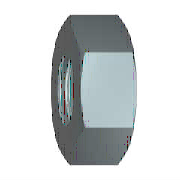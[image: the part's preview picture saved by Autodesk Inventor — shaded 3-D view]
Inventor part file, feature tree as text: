
AUTODESK INVENTOR PART (.ipt)
format: ipt  version: 2024 (Build 280153000, 153)  size: 162,304 bytes
history: native  units: mm (DEFAULTED — no unit token found)
features: other x2, extrude x1, hole x1, plane x1
ambient origin geometry x7: Origin, YZ Plane, XZ Plane, X Axis, Y Axis, Z Axis, Center Point
bodies: Solid1 (feature_tree)
feature tree (5):
  extrude  "Базовый элемент"  Depth=2.886751mm
  other  "Фаска1"
  hole  "Резьба"  [1 undecoded]
  other  "Work Axis1"
  plane  "Work Plane1"
note: 1 required parameter value undecoded (feature->parameter linkage not recoverable at this tier; creation-order binding heuristic only, values carry confidence <= 0.55)
